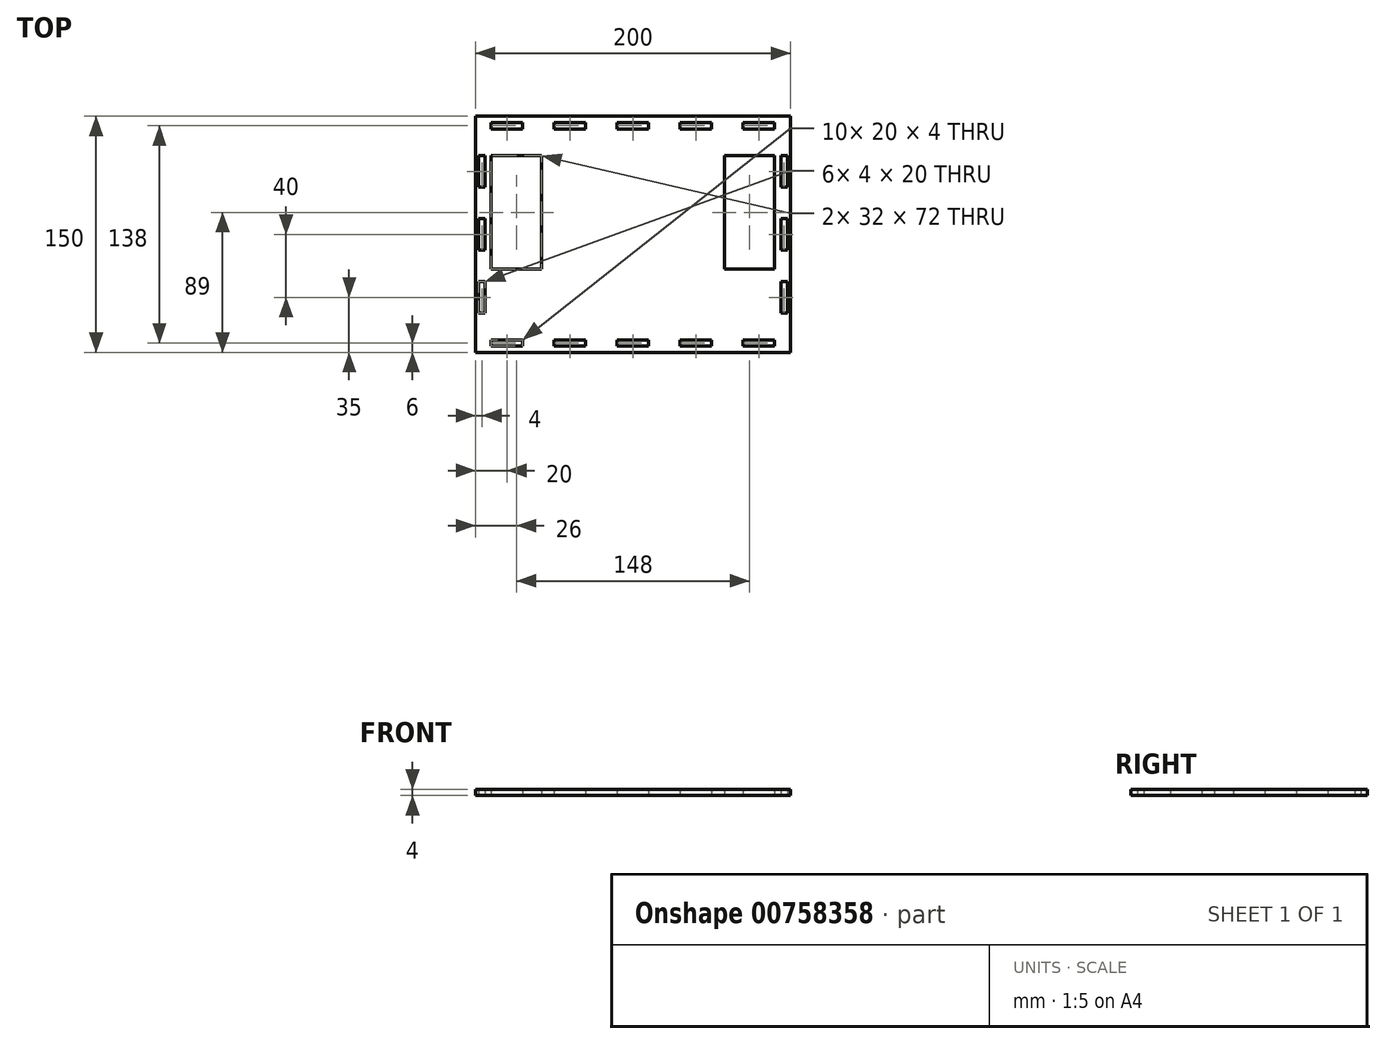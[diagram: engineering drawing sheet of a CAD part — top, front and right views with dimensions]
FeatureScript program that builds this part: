
annotation { "Feature Type Name" : "Feature", "Feature Type Description" : "" }
export const myFeature = defineFeature(function(context is Context, id is Id, definition is map)
    precondition{}
    {
        {
            var Q0;
            Q0=qCreatedBy(makeId("Top.planeOp"),FACE);
            var sketch = newSketch(context, id + "F0", { "sketchPlane" : qUnion([Q0])});
            skLineSegment(sketch, "E0.bottom", {"start": v(100, 75) * mm, "end": v(-100, 75) * mm});
            skLineSegment(sketch, "E0.top", {"start": v(100, -75) * mm, "end": v(-100, -75) * mm});
            skLineSegment(sketch, "E0.left", {"start": v(100, 75) * mm, "end": v(100, -75) * mm});
            skLineSegment(sketch, "E0.right", {"start": v(-100, 75) * mm, "end": v(-100, -75) * mm});
            skPoint(sketch, "E0.middle", {"position": v(0, 0) * mm});
            skPoint(sketch, "E1", {"position": v(0, 75) * mm});
            skPoint(sketch, "E2", {"position": v(100, 0) * mm});
            skLineSegment(sketch, "E3", {"start": v(10, 75) * mm, "end": v(30, 75) * mm});
            skPoint(sketch, "E4.endSnap0", {"position": v(0, -75) * mm});
            skLineSegment(sketch, "E5", {"start": v(100, -10) * mm, "end": v(100, -30) * mm});
            skLineSegment(sketch, "E6", {"start": v(100, -50) * mm, "end": v(100, -70) * mm});
            skLineSegment(sketch, "E7.bottom", {"start": v(-90, 50) * mm, "end": v(-58, 50) * mm});
            skLineSegment(sketch, "E7.top", {"start": v(-90, -22) * mm, "end": v(-58, -22) * mm});
            skLineSegment(sketch, "E7.left", {"start": v(-90, 50) * mm, "end": v(-90, -22) * mm});
            skLineSegment(sketch, "E7.right", {"start": v(-58, 50) * mm, "end": v(-58, -22) * mm});
            skLineSegment(sketch, "E8.MirrorCS", {"start": v(58, 50) * mm, "end": v(58, -22) * mm});
            skLineSegment(sketch, "E9.MirrorCS", {"start": v(90, 50) * mm, "end": v(58, 50) * mm});
            skLineSegment(sketch, "E10.MirrorCS", {"start": v(90, 50) * mm, "end": v(90, -22) * mm});
            skLineSegment(sketch, "E11.MirrorCS", {"start": v(90, -22) * mm, "end": v(58, -22) * mm});
            skLineSegment(sketch, "E12.bottom", {"start": v(-90, 71) * mm, "end": v(-70, 71) * mm});
            skLineSegment(sketch, "E12.top", {"start": v(-90, 67) * mm, "end": v(-70, 67) * mm});
            skLineSegment(sketch, "E12.left", {"start": v(-90, 71) * mm, "end": v(-90, 67) * mm});
            skLineSegment(sketch, "E12.right", {"start": v(-70, 71) * mm, "end": v(-70, 67) * mm});
            skLineSegment(sketch, "E13.1.0.0", {"start": v(-50, 71) * mm, "end": v(-30, 71) * mm});
            skLineSegment(sketch, "E13.1.0.1", {"start": v(-50, 67) * mm, "end": v(-30, 67) * mm});
            skLineSegment(sketch, "E13.1.0.2", {"start": v(-30, 71) * mm, "end": v(-30, 67) * mm});
            skLineSegment(sketch, "E13.1.0.3", {"start": v(-50, 71) * mm, "end": v(-50, 67) * mm});
            skLineSegment(sketch, "E13.2.0.0", {"start": v(-10, 71) * mm, "end": v(10, 71) * mm});
            skLineSegment(sketch, "E13.2.0.1", {"start": v(-10, 67) * mm, "end": v(10, 67) * mm});
            skLineSegment(sketch, "E13.2.0.2", {"start": v(10, 71) * mm, "end": v(10, 67) * mm});
            skLineSegment(sketch, "E13.2.0.3", {"start": v(-10, 71) * mm, "end": v(-10, 67) * mm});
            skLineSegment(sketch, "E13.3.0.0", {"start": v(30, 71) * mm, "end": v(50, 71) * mm});
            skLineSegment(sketch, "E13.3.0.1", {"start": v(30, 67) * mm, "end": v(50, 67) * mm});
            skLineSegment(sketch, "E13.3.0.2", {"start": v(50, 71) * mm, "end": v(50, 67) * mm});
            skLineSegment(sketch, "E13.3.0.3", {"start": v(30, 71) * mm, "end": v(30, 67) * mm});
            skLineSegment(sketch, "E13.4.0.0", {"start": v(70, 71) * mm, "end": v(90, 71) * mm});
            skLineSegment(sketch, "E13.4.0.1", {"start": v(70, 67) * mm, "end": v(90, 67) * mm});
            skLineSegment(sketch, "E13.4.0.2", {"start": v(90, 71) * mm, "end": v(90, 67) * mm});
            skLineSegment(sketch, "E13.4.0.3", {"start": v(70, 71) * mm, "end": v(70, 67) * mm});
            skLineSegment(sketch, "E13.direction1", {"start": v(-90, 71) * mm, "end": v(-50, 71) * mm, "construction": true});
            skPoint(sketch, "E14", {"position": v(-100, 0) * mm});
            skLineSegment(sketch, "E15", {"start": v(-98, 0) * mm, "end": v(-98, 10) * mm});
            skLineSegment(sketch, "E16", {"start": v(-98, 0) * mm, "end": v(-98, -10) * mm});
            skLineSegment(sketch, "E17", {"start": v(-98, -10) * mm, "end": v(-94, -10) * mm});
            skLineSegment(sketch, "E18", {"start": v(-94, 10) * mm, "end": v(-98, 10) * mm});
            skLineSegment(sketch, "E19", {"start": v(-94, 0) * mm, "end": v(-94, 10) * mm});
            skLineSegment(sketch, "E20", {"start": v(-94, -10) * mm, "end": v(-94, 0) * mm});
            skLineSegment(sketch, "E21.0.1.0", {"start": v(-98, 40) * mm, "end": v(-98, 50) * mm});
            skLineSegment(sketch, "E21.0.1.1", {"start": v(-94, 40) * mm, "end": v(-94, 50) * mm});
            skLineSegment(sketch, "E21.0.1.2", {"start": v(-94, 50) * mm, "end": v(-98, 50) * mm});
            skLineSegment(sketch, "E21.0.1.3", {"start": v(-98, 40) * mm, "end": v(-98, 30) * mm});
            skLineSegment(sketch, "E21.0.1.4", {"start": v(-98, 30) * mm, "end": v(-94, 30) * mm});
            skLineSegment(sketch, "E21.0.1.5", {"start": v(-94, 30) * mm, "end": v(-94, 40) * mm});
            skLineSegment(sketch, "E21.direction1", {"start": v(-98, 0) * mm, "end": v(-73, 0) * mm, "construction": true});
            skLineSegment(sketch, "E22.MirrorCS", {"start": v(-94, 0) * mm, "end": v(-94, -10) * mm});
            skLineSegment(sketch, "E23.MirrorCS", {"start": v(-94, -30) * mm, "end": v(-94, -40) * mm});
            skLineSegment(sketch, "E24.MirrorCS", {"start": v(-98, -30) * mm, "end": v(-94, -30) * mm});
            skLineSegment(sketch, "E25.MirrorCS", {"start": v(-98, -40) * mm, "end": v(-98, -50) * mm});
            skLineSegment(sketch, "E26.MirrorCS", {"start": v(-94, -40) * mm, "end": v(-94, -50) * mm});
            skLineSegment(sketch, "E27", {"start": v(-98, -40) * mm, "end": v(-98, -30) * mm});
            skLineSegment(sketch, "E28", {"start": v(-98, -50) * mm, "end": v(-94, -50) * mm});
            skLineSegment(sketch, "E29.MirrorCS", {"start": v(94, 0) * mm, "end": v(94, -10) * mm});
            skLineSegment(sketch, "E30.MirrorCS", {"start": v(98, 0) * mm, "end": v(98, -10) * mm});
            skLineSegment(sketch, "E31.MirrorCS", {"start": v(98, 0) * mm, "end": v(98, 10) * mm});
            skLineSegment(sketch, "E32.MirrorCS", {"start": v(94, 0) * mm, "end": v(94, 10) * mm});
            skLineSegment(sketch, "E33.MirrorCS", {"start": v(94, 10) * mm, "end": v(98, 10) * mm});
            skLineSegment(sketch, "E34.MirrorCS", {"start": v(98, -10) * mm, "end": v(94, -10) * mm});
            skLineSegment(sketch, "E35.MirrorCS", {"start": v(94, -30) * mm, "end": v(94, -40) * mm});
            skLineSegment(sketch, "E36.MirrorCS", {"start": v(94, -40) * mm, "end": v(94, -50) * mm});
            skLineSegment(sketch, "E37.MirrorCS", {"start": v(98, -40) * mm, "end": v(98, -50) * mm});
            skLineSegment(sketch, "E38.MirrorCS", {"start": v(98, -40) * mm, "end": v(98, -30) * mm});
            skLineSegment(sketch, "E39.MirrorCS", {"start": v(98, -30) * mm, "end": v(94, -30) * mm});
            skLineSegment(sketch, "E40.MirrorCS", {"start": v(98, -50) * mm, "end": v(94, -50) * mm});
            skLineSegment(sketch, "E41.MirrorCS", {"start": v(98, 30) * mm, "end": v(94, 30) * mm});
            skLineSegment(sketch, "E42.MirrorCS", {"start": v(98, 40) * mm, "end": v(98, 30) * mm});
            skLineSegment(sketch, "E43.MirrorCS", {"start": v(94, 30) * mm, "end": v(94, 40) * mm});
            skLineSegment(sketch, "E44.MirrorCS", {"start": v(98, 40) * mm, "end": v(98, 50) * mm});
            skLineSegment(sketch, "E45.MirrorCS", {"start": v(94, 40) * mm, "end": v(94, 50) * mm});
            skLineSegment(sketch, "E46.MirrorCS", {"start": v(94, 50) * mm, "end": v(98, 50) * mm});
            skLineSegment(sketch, "E47.MirrorCS", {"start": v(-10, -67) * mm, "end": v(10, -67) * mm});
            skLineSegment(sketch, "E48.MirrorCS", {"start": v(-10, -71) * mm, "end": v(10, -71) * mm});
            skLineSegment(sketch, "E49.MirrorCS", {"start": v(-10, -71) * mm, "end": v(-10, -67) * mm});
            skLineSegment(sketch, "E50.MirrorCS", {"start": v(10, -71) * mm, "end": v(10, -67) * mm});
            skLineSegment(sketch, "E51.MirrorCS", {"start": v(30, -71) * mm, "end": v(30, -67) * mm});
            skLineSegment(sketch, "E52.MirrorCS", {"start": v(50, -71) * mm, "end": v(50, -67) * mm});
            skLineSegment(sketch, "E53.MirrorCS", {"start": v(30, -71) * mm, "end": v(50, -71) * mm});
            skLineSegment(sketch, "E54.MirrorCS", {"start": v(30, -67) * mm, "end": v(50, -67) * mm});
            skLineSegment(sketch, "E55.MirrorCS", {"start": v(70, -71) * mm, "end": v(70, -67) * mm});
            skLineSegment(sketch, "E56.MirrorCS", {"start": v(70, -71) * mm, "end": v(90, -71) * mm});
            skLineSegment(sketch, "E57.MirrorCS", {"start": v(70, -67) * mm, "end": v(90, -67) * mm});
            skLineSegment(sketch, "E58.MirrorCS", {"start": v(90, -71) * mm, "end": v(90, -67) * mm});
            skLineSegment(sketch, "E59.MirrorCS", {"start": v(-90, -67) * mm, "end": v(-70, -67) * mm});
            skLineSegment(sketch, "E60.MirrorCS", {"start": v(-90, -71) * mm, "end": v(-90, -67) * mm});
            skLineSegment(sketch, "E61.MirrorCS", {"start": v(-70, -71) * mm, "end": v(-70, -67) * mm});
            skLineSegment(sketch, "E62.MirrorCS", {"start": v(-50, -71) * mm, "end": v(-50, -67) * mm});
            skLineSegment(sketch, "E63.MirrorCS", {"start": v(-50, -67) * mm, "end": v(-30, -67) * mm});
            skLineSegment(sketch, "E64.MirrorCS", {"start": v(-30, -71) * mm, "end": v(-30, -67) * mm});
            skLineSegment(sketch, "E65.MirrorCS", {"start": v(-50, -71) * mm, "end": v(-30, -71) * mm});
            skLineSegment(sketch, "E66", {"start": v(-90, -71) * mm, "end": v(-70, -71) * mm});
            skSolve(sketch);
        }
        {
            var Q0;
            {var subQ5=sQuery(id+"F0.wireOp",EDGE,"E0.top");Q0=makeQuery(id+"F0.imprint","IMPRINT",FACE,{"disambiguationData":[TD([[makeQuery(id+"F0.imprint","IMPRINT",EDGE,{"derivedFrom":subQ5}),-1.0]])]});}
            extrude(context, id + "F1", {"entities" : qUnion([Q0]), "depth" : 4 * mm});
        }
    });
